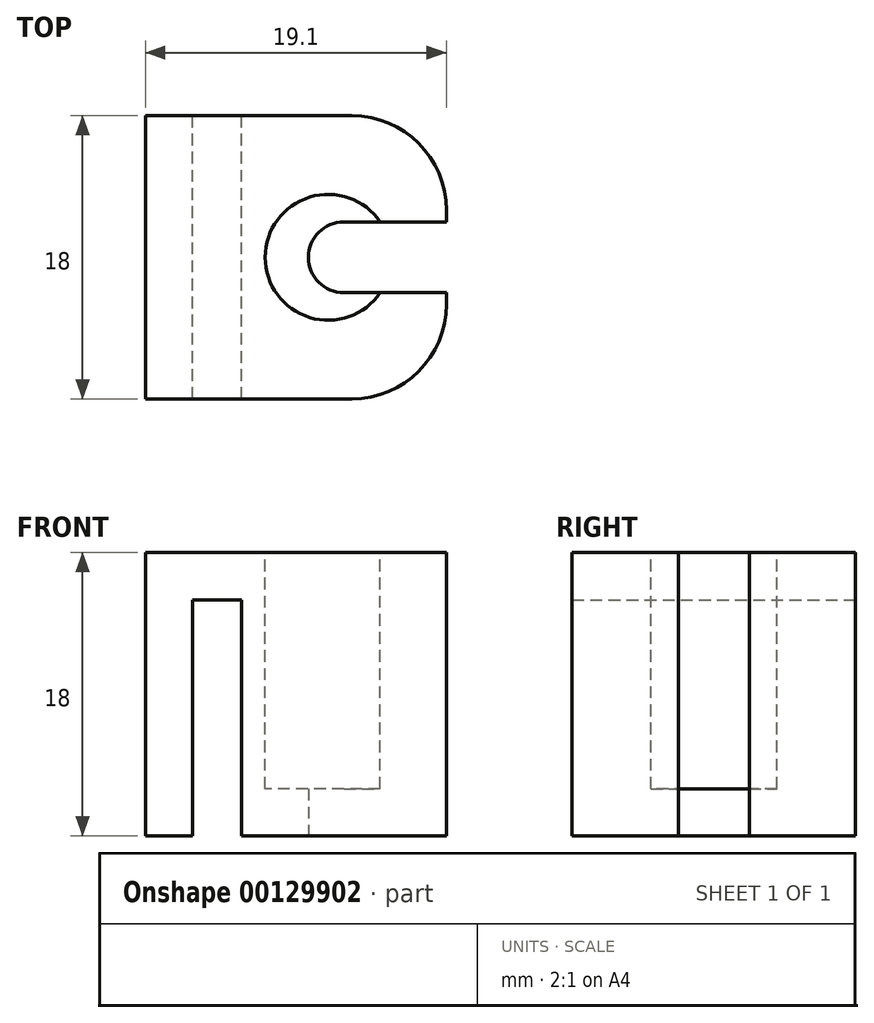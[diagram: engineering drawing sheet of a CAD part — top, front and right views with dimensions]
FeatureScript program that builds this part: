
annotation { "Feature Type Name" : "Feature", "Feature Type Description" : "" }
export const myFeature = defineFeature(function(context is Context, id is Id, definition is map)
    precondition{}
    {
        {
            var Q0;
            Q0=qCreatedBy(makeId("Front.planeOp"),FACE);
            var sketch = newSketch(context, id + "F0", { "sketchPlane" : qUnion([Q0])});
            skLineSegment(sketch, "E0", {"start": v(-19.1, 0) * mm, "end": v(-19.1, 18) * mm});
            skLineSegment(sketch, "E1", {"start": v(-19.1, 18) * mm, "end": v(0, 18) * mm});
            skLineSegment(sketch, "E2", {"start": v(0, 18) * mm, "end": v(0, 0) * mm});
            skLineSegment(sketch, "E3", {"start": v(0, 0) * mm, "end": v(-13, 0) * mm});
            skLineSegment(sketch, "E4", {"start": v(-13, 0) * mm, "end": v(-13, 15) * mm});
            skLineSegment(sketch, "E5", {"start": v(-13, 15) * mm, "end": v(-16.1, 15) * mm});
            skLineSegment(sketch, "E6", {"start": v(-16.1, 15) * mm, "end": v(-16.1, 0) * mm});
            skLineSegment(sketch, "E7", {"start": v(-16.1, 0) * mm, "end": v(-19.1, 0) * mm});
            skSolve(sketch);
        }
        {
            var Q0;
            Q0 = qSketchRegion(id + "F0", true);
            extrude(context, id + "F1", {"entities" : qUnion([Q0]), "depth" : 18 * mm});
        }
        {
            var Q0;
            Q0=makeQuery(id+"F1.opExtrude","SWEPT_FACE",FACE,{"disambiguationData":[OSD([sQuery(id+"F0.wireOp",EDGE,"E1")])]});
            var sketch = newSketch(context, id + "F2", { "sketchPlane" : qUnion([Q0])});
            skLineSegment(sketch, "E8", {"start": v(-15, 0) * mm, "end": v(-15, -18) * mm, "construction": true});
            skPoint(sketch, "E9", {"position": v(-15, -9) * mm});
            skPoint(sketch, "E10", {"position": v(-7.5, -9) * mm});
            skLineSegment(sketch, "E11", {"start": v(-15, 0) * mm, "end": v(0, 0) * mm, "construction": true});
            skPoint(sketch, "E12", {"position": v(-7.5, 0) * mm});
            skCircle(sketch, "E13", {"center": v(-7.5, -9) * mm, "radius": 4 * mm});
            skSolve(sketch);
        }
        {
            var Q0;
            Q0 = qSketchRegion(id + "F2", true);
            extrude(context, id + "F3", {"entities" : qUnion([Q0]), "operationType" : NewBodyOperationType.REMOVE, "oppositeDirection" : true, "depth" : 15 * mm});
        }
        {
            var Q0;
            Q0=makeQuery(id+"F1.opExtrude","SWEPT_FACE",FACE,{"disambiguationData":[OSD([sQuery(id+"F0.wireOp",EDGE,"E3")])]});
            var sketch = newSketch(context, id + "F4", { "sketchPlane" : qUnion([Q0])});
            skPoint(sketch, "E14", {"position": v(-6.5, 18) * mm});
            skPoint(sketch, "E15", {"position": v(-13, 9) * mm});
            skCircle(sketch, "E16", {"center": v(-6.5, 9) * mm, "radius": 2.25 * mm});
            skLineSegment(sketch, "E17", {"start": v(-6.5, 11.25) * mm, "end": v(0, 11.25) * mm});
            skLineSegment(sketch, "E18", {"start": v(0, 11.25) * mm, "end": v(0, 6.75) * mm});
            skLineSegment(sketch, "E19", {"start": v(0, 6.75) * mm, "end": v(-6.5, 6.75) * mm});
            skSolve(sketch);
        }
        {
            var Q0;
            Q0 = qSketchRegion(id + "F4", true);
            var Q1;
            Q1=makeQuery(id+"F1.opExtrude","SWEPT_BODY",BODY,{"disambiguationData":[OSD([sQuery(id+"F0.wireOp",EDGE,"E0"),sQuery(id+"F0.wireOp",EDGE,"E1"),sQuery(id+"F0.wireOp",EDGE,"E2"),sQuery(id+"F0.wireOp",EDGE,"E3"),sQuery(id+"F0.wireOp",EDGE,"E4"),sQuery(id+"F0.wireOp",EDGE,"E5"),sQuery(id+"F0.wireOp",EDGE,"E6"),sQuery(id+"F0.wireOp",EDGE,"E7")])]});
            extrude(context, id + "F5", {"entities" : qUnion([Q0]), "operationType" : NewBodyOperationType.REMOVE, "endBound" : BoundingType.UP_TO_BODY, "oppositeDirection" : true, "endBoundEntityBody" : qUnion([Q1]), "depth" : 25 * mm});
        }
        {
            var Q0;
            Q0=makeQuery(id+"F1.opExtrude","CAP_EDGE",EDGE,{"disambiguationData":[OSD([sQuery(id+"F0.wireOp",EDGE,"E2")])],"isStart":false});
            var Q1;
            Q1=makeQuery(id+"F1.opExtrude","CAP_EDGE",EDGE,{"disambiguationData":[OSD([sQuery(id+"F0.wireOp",EDGE,"E2")])],"isStart":true});
            fillet(context, id + "F6", {"entities" : qUnion([Q0, Q1]), "radius" : 6 * mm, "tangentPropagation" : true, "allowEdgeOverflow" : false});
        }
    });
